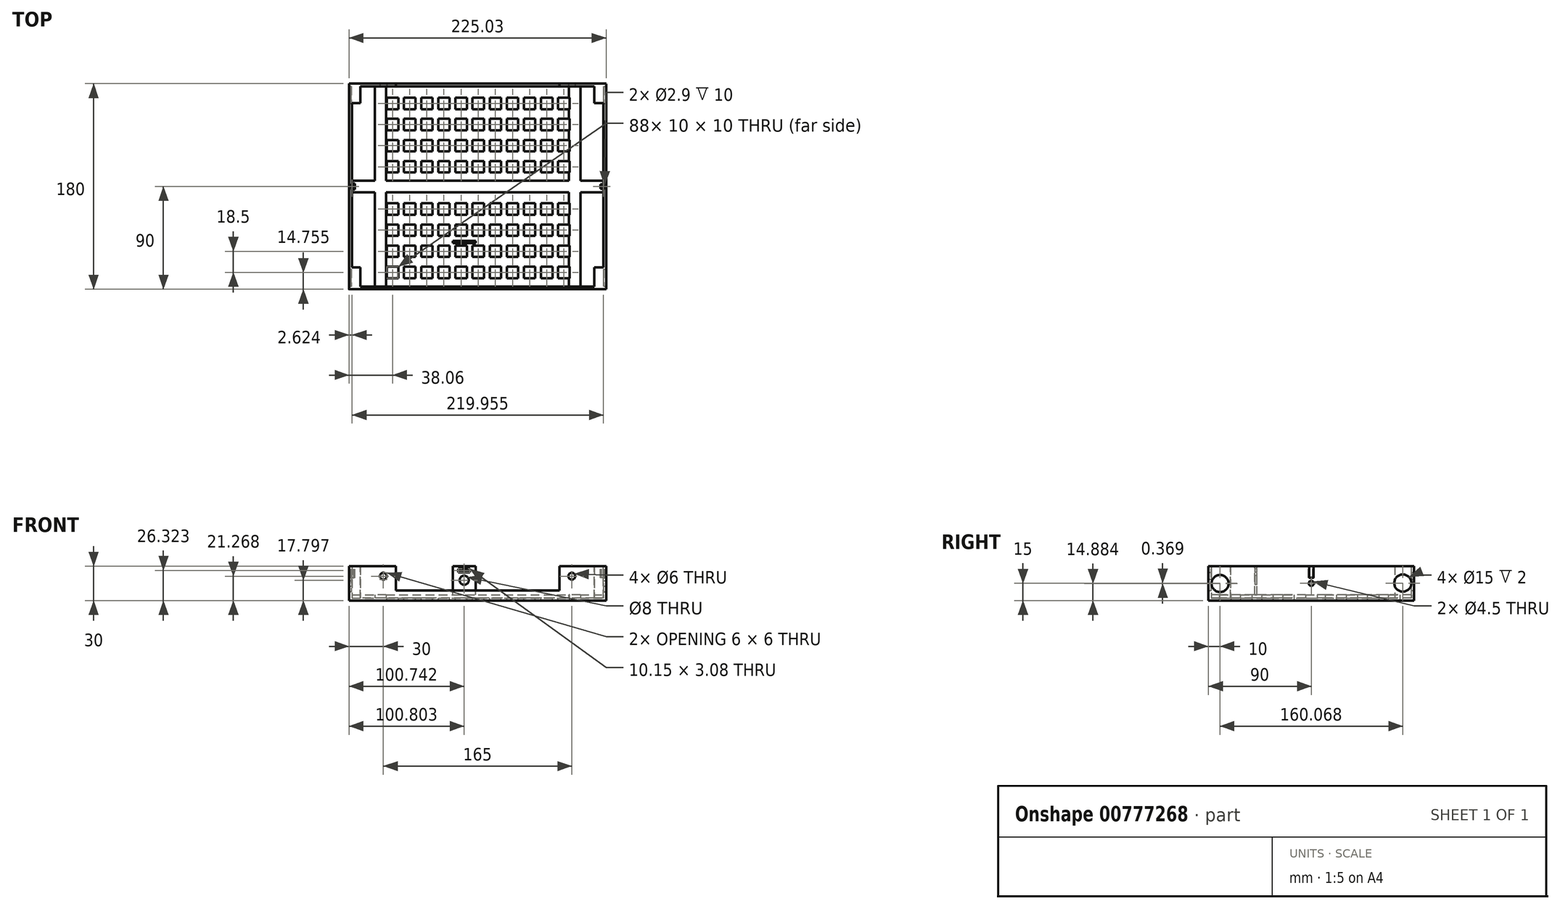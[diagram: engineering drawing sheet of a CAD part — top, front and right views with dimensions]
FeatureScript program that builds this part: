
annotation { "Feature Type Name" : "Feature", "Feature Type Description" : "" }
export const myFeature = defineFeature(function(context is Context, id is Id, definition is map)
    precondition{}
    {
        {
            var Q0;
            Q0=qCreatedBy(makeId("Top.planeOp"),FACE);
            var sketch = newSketch(context, id + "F0", { "sketchPlane" : qUnion([Q0])});
            skLineSegment(sketch, "E0.bottom", {"start": v(112.5, -90) * mm, "end": v(-112.5, -90) * mm});
            skLineSegment(sketch, "E0.top", {"start": v(112.5, 90) * mm, "end": v(-112.5, 90) * mm});
            skLineSegment(sketch, "E0.left", {"start": v(112.5, -90) * mm, "end": v(112.5, 90) * mm});
            skLineSegment(sketch, "E0.right", {"start": v(-112.5, -90) * mm, "end": v(-112.5, 90) * mm});
            skPoint(sketch, "E0.middle", {"position": v(0, 0) * mm});
            skSolve(sketch);
        }
        {
            var Q0;
            Q0=makeQuery(id+"F0.imprint","IMPRINT",FACE,{"disambiguationData":[TD([[makeQuery(id+"F0.imprint","IMPRINT",EDGE,{"derivedFrom":sQuery(id+"F0.wireOp",EDGE,"E0.bottom")}),-1.0]])]});
            extrude(context, id + "F1", {"entities" : qUnion([Q0]), "depth" : 30 * mm, "offsetDistance" : 25 * mm});
        }
        {
            var Q0;
            Q0=makeQuery(id+"F1.opExtrude","CAP_FACE",FACE,{"disambiguationData":[OSD([sQuery(id+"F0.wireOp",EDGE,"E0.bottom"),sQuery(id+"F0.wireOp",EDGE,"E0.top"),sQuery(id+"F0.wireOp",EDGE,"E0.left"),sQuery(id+"F0.wireOp",EDGE,"E0.right")])],"isStart":false});
            var sketch = newSketch(context, id + "F2", { "sketchPlane" : qUnion([Q0])});
            skLineSegment(sketch, "E1.bottom", {"start": v(110, -87.5) * mm, "end": v(-110, -87.5) * mm});
            skLineSegment(sketch, "E1.top", {"start": v(110, 87.5) * mm, "end": v(-110, 87.5) * mm});
            skLineSegment(sketch, "E1.left", {"start": v(110, -87.5) * mm, "end": v(110, 87.5) * mm});
            skLineSegment(sketch, "E1.right", {"start": v(-110, -87.5) * mm, "end": v(-110, 87.5) * mm});
            skPoint(sketch, "E1.middle", {"position": v(0, 0) * mm});
            skSolve(sketch);
        }
        {
            var Q0;
            Q0=makeQuery(id+"F2.imprint","IMPRINT",FACE,{"disambiguationData":[TD([[makeQuery(id+"F2.imprint","IMPRINT",EDGE,{"derivedFrom":sQuery(id+"F2.wireOp",EDGE,"E1.bottom")}),-1.0]])]});
            extrude(context, id + "F3", {"entities" : qUnion([Q0]), "operationType" : NewBodyOperationType.REMOVE, "oppositeDirection" : true, "depth" : 28 * mm, "offsetDistance" : 25 * mm});
        }
        {
            var Q0;
            Q0=makeQuery(id+"F1.opExtrude","SWEPT_FACE",FACE,{"disambiguationData":[OSD([sQuery(id+"F0.wireOp",EDGE,"E0.bottom")])]});
            var sketch = newSketch(context, id + "F4", { "sketchPlane" : qUnion([Q0])});
            skLineSegment(sketch, "E2", {"start": v(0, 15) * mm, "end": v(0, 30) * mm, "construction": true});
            skPoint(sketch, "E2.startSnap0", {"position": v(-112.5, 15) * mm});
            skPoint(sketch, "E2.startSnap1", {"position": v(0, 30) * mm});
            skLineSegment(sketch, "E3", {"start": v(0, 15) * mm, "end": v(-112.5, 15) * mm, "construction": true});
            skLineSegment(sketch, "E4", {"start": v(0, 15) * mm, "end": v(112.5, 15) * mm, "construction": true});
            skLineSegment(sketch, "E5", {"start": v(-112.5, 0) * mm, "end": v(-82.5, 0) * mm, "construction": true});
            skLineSegment(sketch, "E6", {"start": v(112.5, 0) * mm, "end": v(82.5, 0) * mm, "construction": true});
            skLineSegment(sketch, "E7", {"start": v(-82.5, 0) * mm, "end": v(-82.5, 30) * mm, "construction": true});
            skLineSegment(sketch, "E8", {"start": v(82.5, 0) * mm, "end": v(82.5, 30) * mm, "construction": true});
            skLineSegment(sketch, "E9", {"start": v(-112.5, 30) * mm, "end": v(-72.5, 30) * mm, "construction": true});
            skLineSegment(sketch, "E10", {"start": v(112.5, 30) * mm, "end": v(72.5, 30) * mm, "construction": true});
            skLineSegment(sketch, "E11", {"start": v(-112.5, 0) * mm, "end": v(-112.5, 10) * mm, "construction": true});
            skLineSegment(sketch, "E12", {"start": v(-112.5, 10) * mm, "end": v(112.5, 10) * mm, "construction": true});
            skLineSegment(sketch, "E13", {"start": v(-22.5, 30) * mm, "end": v(-22.5, 0) * mm, "construction": true});
            skLineSegment(sketch, "E14", {"start": v(22.5, 30) * mm, "end": v(22.5, 0) * mm, "construction": true});
            skFitSpline(sketch, "E15", {"points": [v(-72.5, 30) * mm, v(-71.2, 15) * mm, v(-22.5, 10) * mm], "startDerivative": vector(-3.64, -53.35) * mm, "endDerivative": vector(76.18, -37.14) * mm});
            skFitSpline(sketch, "E16", {"points": [v(72.5, 30) * mm, v(72.49, 15) * mm, v(22.5, 10) * mm], "startDerivative": vector(-2.42, -56.98) * mm, "endDerivative": vector(-66.73, -35.72) * mm});
            skLineSegment(sketch, "E17", {"start": v(-22.5, 10) * mm, "end": v(-22.5, 0) * mm});
            skLineSegment(sketch, "E18", {"start": v(22.5, 10) * mm, "end": v(22.5, 0) * mm});
            skLineSegment(sketch, "E19", {"start": v(-22.5, 10) * mm, "end": v(22.5, 10) * mm});
            skLineSegment(sketch, "E20", {"start": v(112.5, 21.27) * mm, "end": v(-112.5, 21.27) * mm, "construction": true});
            skCircle(sketch, "E21", {"center": v(82.5, 21.27) * mm, "radius": 3 * mm});
            skCircle(sketch, "E22", {"center": v(-82.5, 21.27) * mm, "radius": 3 * mm});
            skSolve(sketch);
        }
        {
            var Q0;
            Q0=qSketchRegion(id+"F4",true);
            extrude(context, id + "F5", {"entities" : qUnion([Q0]), "operationType" : NewBodyOperationType.REMOVE, "oppositeDirection" : true, "depth" : 2500 * mm, "offsetDistance" : 25 * mm});
        }
        {
            var Q0;
            Q0=makeQuery(id+"F3.boolean.opBoolean","COPY",FACE,{"derivedFrom":makeQuery(id+"F3.opExtrude","CAP_FACE",FACE,{"disambiguationData":[OSD([sQuery(id+"F2.wireOp",EDGE,"E1.bottom"),sQuery(id+"F2.wireOp",EDGE,"E1.top"),sQuery(id+"F2.wireOp",EDGE,"E1.left"),sQuery(id+"F2.wireOp",EDGE,"E1.right")])],"isStart":false})});
            var sketch = newSketch(context, id + "F6", { "sketchPlane" : qUnion([Q0])});
            skLineSegment(sketch, "E23", {"start": v(-110, 87.5) * mm, "end": v(-90, 87.5) * mm, "construction": true});
            skLineSegment(sketch, "E24.bottom", {"start": v(-90, 87.5) * mm, "end": v(-80, 87.5) * mm});
            skLineSegment(sketch, "E24.top", {"start": v(-90, -87.5) * mm, "end": v(-80, -87.5) * mm});
            skLineSegment(sketch, "E24.left", {"start": v(-90, 87.5) * mm, "end": v(-90, -87.5) * mm});
            skLineSegment(sketch, "E24.right", {"start": v(-80, 87.5) * mm, "end": v(-80, -87.5) * mm});
            skLineSegment(sketch, "E25", {"start": v(110, 87.5) * mm, "end": v(90, 87.5) * mm, "construction": true});
            skLineSegment(sketch, "E26.bottom", {"start": v(90, 87.5) * mm, "end": v(80, 87.5) * mm});
            skLineSegment(sketch, "E26.top", {"start": v(90, -87.5) * mm, "end": v(80, -87.5) * mm});
            skLineSegment(sketch, "E26.left", {"start": v(90, 87.5) * mm, "end": v(90, -87.5) * mm});
            skLineSegment(sketch, "E26.right", {"start": v(80, 87.5) * mm, "end": v(80, -87.5) * mm});
            skLineSegment(sketch, "E27.bottom", {"start": v(-110, 5) * mm, "end": v(110, 5) * mm});
            skLineSegment(sketch, "E27.top", {"start": v(-110, -5) * mm, "end": v(110, -5) * mm});
            skLineSegment(sketch, "E27.left", {"start": v(-110, 5) * mm, "end": v(-110, -5) * mm});
            skLineSegment(sketch, "E27.right", {"start": v(110, 5) * mm, "end": v(110, -5) * mm});
            skPoint(sketch, "E27.middle", {"position": v(0, 0) * mm});
            skSolve(sketch);
        }
        {
            var Q0;
            Q0=makeQuery(id+"F6.imprint","IMPRINT",FACE,{"disambiguationData":[TD([[makeQuery(id+"F6.imprint","IMPRINT",EDGE,{"derivedFrom":sQuery(id+"F6.wireOp",EDGE,"E24.bottom")}),1.0]])]});
            var Q1;
            Q1=makeQuery(id+"F6.imprint","IMPRINT",FACE,{"disambiguationData":[TD([[makeQuery(id+"F6.imprint","IMPRINT",EDGE,{"derivedFrom":sQuery(id+"F6.wireOp",EDGE,"E26.bottom")}),1.0]])]});
            var Q2;
            {var subQ5=sQuery(id+"F6.wireOp",EDGE,"E27.left");Q2=makeQuery(id+"F6.imprint","IMPRINT",FACE,{"disambiguationData":[TD([[makeQuery(id+"F6.imprint","IMPRINT",EDGE,{"derivedFrom":subQ5}),-1.0]])]});}
            var Q3;
            {var subQ0=sQuery(id+"F6.wireOp",EDGE,"E27.bottom");var subQ1=sQuery(id+"F6.wireOp",EDGE,"E24.left");var subQ2=makeQuery(id+"F6.imprint","INTERSECT",VERTEX,{"derivedFrom":[subQ1,subQ0]});Q3=makeQuery(id+"F6.imprint","IMPRINT",FACE,{"disambiguationData":[TD([[makeQuery(id+"F6.imprint","IMPRINT",EDGE,{"disambiguationData":[TD([[subQ2,-1.0]])],"derivedFrom":subQ1}),1.0]])]});}
            var Q4;
            {var subQ0=sQuery(id+"F6.wireOp",EDGE,"E24.top");Q4=makeQuery(id+"F6.imprint","IMPRINT",FACE,{"disambiguationData":[TD([[makeQuery(id+"F6.imprint","IMPRINT",EDGE,{"derivedFrom":subQ0}),-1.0]])]});}
            var Q5;
            {var subQ0=sQuery(id+"F6.wireOp",EDGE,"E27.bottom");var subQ1=sQuery(id+"F6.wireOp",EDGE,"E24.right");var subQ2=makeQuery(id+"F6.imprint","INTERSECT",VERTEX,{"derivedFrom":[subQ1,subQ0]});Q5=makeQuery(id+"F6.imprint","IMPRINT",FACE,{"disambiguationData":[TD([[makeQuery(id+"F6.imprint","IMPRINT",EDGE,{"disambiguationData":[TD([[subQ2,-1.0]])],"derivedFrom":subQ1}),1.0]])]});}
            var Q6;
            {var subQ0=sQuery(id+"F6.wireOp",EDGE,"E27.bottom");var subQ1=sQuery(id+"F6.wireOp",EDGE,"E26.left");var subQ2=makeQuery(id+"F6.imprint","INTERSECT",VERTEX,{"derivedFrom":[subQ1,subQ0]});Q6=makeQuery(id+"F6.imprint","IMPRINT",FACE,{"disambiguationData":[TD([[makeQuery(id+"F6.imprint","IMPRINT",EDGE,{"disambiguationData":[TD([[subQ2,-1.0]])],"derivedFrom":subQ1}),-1.0]])]});}
            var Q7;
            {var subQ0=sQuery(id+"F6.wireOp",EDGE,"E26.top");Q7=makeQuery(id+"F6.imprint","IMPRINT",FACE,{"disambiguationData":[TD([[makeQuery(id+"F6.imprint","IMPRINT",EDGE,{"derivedFrom":subQ0}),-1.0]])]});}
            var Q8;
            {var subQ5=sQuery(id+"F6.wireOp",EDGE,"E27.right");Q8=makeQuery(id+"F6.imprint","IMPRINT",FACE,{"disambiguationData":[TD([[makeQuery(id+"F6.imprint","IMPRINT",EDGE,{"derivedFrom":subQ5}),1.0]])]});}
            extrude(context, id + "F7", {"entities" : qUnion([Q0, Q1, Q2, Q3, Q4, Q5, Q6, Q7, Q8]), "depth" : 3 * mm, "offsetDistance" : 25 * mm});
        }
        {
            var Q0;
            Q0=makeQuery(id+"F1.opExtrude","SWEPT_FACE",FACE,{"disambiguationData":[OSD([sQuery(id+"F0.wireOp",EDGE,"E0.left")])]});
            var sketch = newSketch(context, id + "F8", { "sketchPlane" : qUnion([Q0])});
            skLineSegment(sketch, "E28", {"start": v(0, 30) * mm, "end": v(0, 0) * mm, "construction": true});
            skLineSegment(sketch, "E29", {"start": v(-90, 15) * mm, "end": v(90, 15) * mm, "construction": true});
            skCircle(sketch, "E30", {"center": v(0, 15) * mm, "radius": 2.25 * mm});
            skSolve(sketch);
        }
        {
            var Q0;
            Q0=makeQuery(id+"F8.imprint","IMPRINT",FACE,{"disambiguationData":[TD([[makeQuery(id+"F8.imprint","IMPRINT",EDGE,{"derivedFrom":sQuery(id+"F8.wireOp",EDGE,"E30")}),1.0]])]});
            extrude(context, id + "F9", {"entities" : qUnion([Q0]), "operationType" : NewBodyOperationType.REMOVE, "endBound" : BoundingType.THROUGH_ALL, "oppositeDirection" : true, "depth" : 25 * mm, "offsetDistance" : 25 * mm});
        }
        {
            var Q0;
            Q0=makeQuery(id+"F1.opExtrude","SWEPT_FACE",FACE,{"disambiguationData":[OSD([sQuery(id+"F0.wireOp",EDGE,"E0.top")])]});
            var sketch = newSketch(context, id + "F10", { "sketchPlane" : qUnion([Q0])});
            skLineSegment(sketch, "E31.bottom", {"start": v(71.59, 8.69) * mm, "end": v(-71.59, 8.69) * mm});
            skLineSegment(sketch, "E31.top", {"start": v(71.59, 51.31) * mm, "end": v(-71.59, 51.31) * mm});
            skLineSegment(sketch, "E31.left", {"start": v(71.59, 8.69) * mm, "end": v(71.59, 51.31) * mm});
            skLineSegment(sketch, "E31.right", {"start": v(-71.59, 8.69) * mm, "end": v(-71.59, 51.31) * mm});
            skPoint(sketch, "E31.middle", {"position": v(0, 30) * mm});
            skSolve(sketch);
        }
        {
            var Q0;
            {var subQ0=sQuery(id+"F10.wireOp",EDGE,"E31.bottom");Q0=makeQuery(id+"F10.imprint","IMPRINT",FACE,{"disambiguationData":[TD([[makeQuery(id+"F10.imprint","IMPRINT",EDGE,{"derivedFrom":subQ0}),-1.0]])]});}
            extrude(context, id + "F11", {"entities" : qUnion([Q0]), "operationType" : NewBodyOperationType.REMOVE, "oppositeDirection" : true, "depth" : 3000 * mm, "offsetDistance" : 25 * mm});
        }
        {
            var Q0;
            Q0=makeQuery(id+"F2.imprint","IMPRINT",FACE,{"disambiguationData":[TD([[makeQuery(id+"F2.imprint","IMPRINT",EDGE,{"derivedFrom":sQuery(id+"F2.wireOp",EDGE,"E1.bottom")}),-1.0]])]});
            var sketch = newSketch(context, id + "F12", { "sketchPlane" : qUnion([Q0])});
            skLineSegment(sketch, "E32.bottom", {"start": v(-112.4, 89.96) * mm, "end": v(-102.7, 89.96) * mm});
            skLineSegment(sketch, "E32.top", {"start": v(-112.4, 72.97) * mm, "end": v(-102.7, 72.97) * mm});
            skLineSegment(sketch, "E32.left", {"start": v(-112.4, 89.96) * mm, "end": v(-112.4, 72.97) * mm});
            skLineSegment(sketch, "E32.right", {"start": v(-102.7, 89.96) * mm, "end": v(-102.7, 72.97) * mm});
            skLineSegment(sketch, "E33.bottom", {"start": v(-112.5, -89.96) * mm, "end": v(-102.68, -89.96) * mm});
            skLineSegment(sketch, "E33.top", {"start": v(-112.5, -70.82) * mm, "end": v(-102.68, -70.82) * mm});
            skLineSegment(sketch, "E33.left", {"start": v(-112.5, -89.96) * mm, "end": v(-112.5, -70.82) * mm});
            skLineSegment(sketch, "E33.right", {"start": v(-102.68, -89.96) * mm, "end": v(-102.68, -70.82) * mm});
            skLineSegment(sketch, "E34.bottom", {"start": v(112.5, 89.98) * mm, "end": v(102.19, 89.98) * mm});
            skLineSegment(sketch, "E34.top", {"start": v(112.5, 72.97) * mm, "end": v(102.19, 72.97) * mm});
            skLineSegment(sketch, "E34.left", {"start": v(112.5, 89.98) * mm, "end": v(112.5, 72.97) * mm});
            skLineSegment(sketch, "E34.right", {"start": v(102.19, 89.98) * mm, "end": v(102.19, 72.97) * mm});
            skLineSegment(sketch, "E35.bottom", {"start": v(112.45, -89.96) * mm, "end": v(102.2, -89.96) * mm});
            skLineSegment(sketch, "E35.top", {"start": v(112.45, -70.67) * mm, "end": v(102.2, -70.67) * mm});
            skLineSegment(sketch, "E35.left", {"start": v(112.45, -89.96) * mm, "end": v(112.45, -70.67) * mm});
            skLineSegment(sketch, "E35.right", {"start": v(102.2, -89.96) * mm, "end": v(102.2, -70.67) * mm});
            skLineSegment(sketch, "E36", {"start": v(-102.7, -93.75) * mm, "end": v(-102.7, 94.08) * mm, "construction": true});
            skLineSegment(sketch, "E37", {"start": v(-116.28, -70.82) * mm, "end": v(124.38, -70.82) * mm, "construction": true});
            skLineSegment(sketch, "E38", {"start": v(-119.93, 72.97) * mm, "end": v(152.22, 72.97) * mm, "construction": true});
            skLineSegment(sketch, "E39", {"start": v(102.19, 97.41) * mm, "end": v(102.19, -106.67) * mm, "construction": true});
            skSolve(sketch);
        }
        {
            var Q0;
            Q0=qSketchRegion(id+"F12",true);
            extrude(context, id + "F13", {"entities" : qUnion([Q0]), "operationType" : NewBodyOperationType.ADD, "oppositeDirection" : true, "depth" : 30 * mm, "offsetDistance" : 25 * mm});
        }
        {
            var Q0;
            Q0=makeQuery(id+"F1.opExtrude","SWEPT_FACE",FACE,{"disambiguationData":[OSD([sQuery(id+"F0.wireOp",EDGE,"E0.right")])]});
            var sketch = newSketch(context, id + "F14", { "sketchPlane" : qUnion([Q0])});
            skLineSegment(sketch, "E40", {"start": v(-80, 30) * mm, "end": v(-80, 0) * mm, "construction": true});
            skLineSegment(sketch, "E41", {"start": v(80, 30) * mm, "end": v(80, 0) * mm, "construction": true});
            skCircle(sketch, "E42", {"center": v(-80, 15) * mm, "radius": 7.5 * mm});
            skCircle(sketch, "E43", {"center": v(80, 15) * mm, "radius": 7.5 * mm});
            skSolve(sketch);
        }
        {
            var Q0;
            Q0=qSketchRegion(id+"F14",true);
            extrude(context, id + "F15", {"entities" : qUnion([Q0]), "operationType" : NewBodyOperationType.REMOVE, "oppositeDirection" : true, "depth" : 2 * mm, "offsetDistance" : 25 * mm});
        }
        {
            var Q0;
            Q0=makeQuery(id+"F8.imprint","IMPRINT",FACE,{"disambiguationData":[TD([[makeQuery(id+"F8.imprint","IMPRINT",EDGE,{"derivedFrom":sQuery(id+"F8.wireOp",EDGE,"E30")}),-1.0]])]});
            var sketch = newSketch(context, id + "F16", { "sketchPlane" : qUnion([Q0])});
            skCircle(sketch, "E44", {"center": v(-79.9, 14.88) * mm, "radius": 7.5 * mm});
            skCircle(sketch, "E45", {"center": v(80.07, 15.25) * mm, "radius": 7.5 * mm});
            skSolve(sketch);
        }
        {
            var Q0;
            Q0=qSketchRegion(id+"F16",true);
            extrude(context, id + "F17", {"entities" : qUnion([Q0]), "operationType" : NewBodyOperationType.REMOVE, "oppositeDirection" : true, "depth" : 2 * mm, "offsetDistance" : 25 * mm});
        }
        {
            var Q0;
            {var subQ0=sQuery(id+"F12.wireOp",EDGE,"E32.right");var subQ17=sQuery(id+"F12.wireOp",EDGE,"E32.top");var subQ18=makeQuery(id+"F12.imprint","INTERSECT",VERTEX,{"derivedFrom":[subQ17,subQ0]});Q0=makeQuery(id+"F12.imprint","IMPRINT",FACE,{"disambiguationData":[TD([[makeQuery(id+"F12.imprint","IMPRINT",EDGE,{"disambiguationData":[TD([[subQ18,1.0]])],"derivedFrom":subQ17}),-1.0]])]});}
            var sketch = newSketch(context, id + "F18", { "sketchPlane" : qUnion([Q0])});
            skLineSegment(sketch, "E46", {"start": v(-21.73, -47.51) * mm, "end": v(-1.73, -47.51) * mm});
            skLineSegment(sketch, "E47", {"start": v(-1.73, -47.51) * mm, "end": v(-1.73, -49.51) * mm});
            skLineSegment(sketch, "E48", {"start": v(-1.73, -49.51) * mm, "end": v(-21.73, -49.51) * mm});
            skLineSegment(sketch, "E49", {"start": v(-21.73, -49.51) * mm, "end": v(-21.73, -47.51) * mm});
            skSolve(sketch);
        }
        {
            var Q0;
            Q0=makeQuery(id+"F18.imprint","IMPRINT",FACE,{"disambiguationData":[TD([[makeQuery(id+"F18.imprint","IMPRINT",EDGE,{"derivedFrom":sQuery(id+"F18.wireOp",EDGE,"E46")}),-1.0]])]});
            extrude(context, id + "F19", {"entities" : qUnion([Q0]), "operationType" : NewBodyOperationType.ADD, "oppositeDirection" : true, "depth" : 25 * mm, "offsetDistance" : 25 * mm});
        }
        {
            var Q0;
            {var subQ0=sQuery(id+"F4.wireOp",EDGE,"E15");Q0=makeQuery(id+"F4.imprint","IMPRINT",FACE,{"disambiguationData":[TD([[makeQuery(id+"F4.imprint","IMPRINT",EDGE,{"derivedFrom":subQ0}),1.0]])]});}
            var sketch = newSketch(context, id + "F20", { "sketchPlane" : qUnion([Q0])});
            skCircle(sketch, "E50", {"center": v(-11.7, 17.8) * mm, "radius": 4 * mm});
            skSolve(sketch);
        }
        {
            var Q0;
            Q0=qSketchRegion(id+"F20",true);
            extrude(context, id + "F21", {"entities" : qUnion([Q0]), "operationType" : NewBodyOperationType.REMOVE, "oppositeDirection" : true, "depth" : 3000 * mm, "offsetDistance" : 25 * mm});
        }
        {
            var Q0;
            {var subQ4=sQuery(id+"F4.wireOp",EDGE,"E15");Q0=makeQuery(id+"F4.imprint","IMPRINT",FACE,{"disambiguationData":[TD([[makeQuery(id+"F4.imprint","IMPRINT",EDGE,{"derivedFrom":subQ4}),-1.0]])]});}
            var sketch = newSketch(context, id + "F22", { "sketchPlane" : qUnion([Q0])});
            skLineSegment(sketch, "E51.bottom", {"start": v(-6.68, 24.78) * mm, "end": v(-16.83, 24.78) * mm});
            skLineSegment(sketch, "E51.top", {"start": v(-6.68, 27.86) * mm, "end": v(-16.83, 27.86) * mm});
            skLineSegment(sketch, "E51.left", {"start": v(-6.68, 24.78) * mm, "end": v(-6.68, 27.86) * mm});
            skLineSegment(sketch, "E51.right", {"start": v(-16.83, 24.78) * mm, "end": v(-16.83, 27.86) * mm});
            skPoint(sketch, "E51.middle", {"position": v(-11.76, 26.32) * mm});
            skSolve(sketch);
        }
        {
            var Q0;
            Q0=qSketchRegion(id+"F22",true);
            extrude(context, id + "F23", {"entities" : qUnion([Q0]), "operationType" : NewBodyOperationType.REMOVE, "oppositeDirection" : true, "depth" : 3000 * mm, "offsetDistance" : 25 * mm});
        }
        {
            var Q0;
            Q0=makeQuery(id+"F0.imprint","IMPRINT",FACE,{"disambiguationData":[TD([[makeQuery(id+"F0.imprint","IMPRINT",EDGE,{"derivedFrom":sQuery(id+"F0.wireOp",EDGE,"E0.bottom")}),-1.0]])]});
            var sketch = newSketch(context, id + "F24", { "sketchPlane" : qUnion([Q0])});
            skLineSegment(sketch, "E52.bottom", {"start": v(-69.44, -80.25) * mm, "end": v(-79.44, -80.25) * mm});
            skLineSegment(sketch, "E52.top", {"start": v(-69.44, -70.25) * mm, "end": v(-79.44, -70.25) * mm});
            skLineSegment(sketch, "E52.left", {"start": v(-69.44, -80.25) * mm, "end": v(-69.44, -70.25) * mm});
            skLineSegment(sketch, "E52.right", {"start": v(-79.44, -80.25) * mm, "end": v(-79.44, -70.25) * mm});
            skPoint(sketch, "E52.middle", {"position": v(-74.44, -75.25) * mm});
            skPoint(sketch, "E53.0.1.0", {"position": v(-74.44, -56.75) * mm});
            skLineSegment(sketch, "E53.0.1.1", {"start": v(-69.44, -61.75) * mm, "end": v(-69.44, -51.75) * mm});
            skLineSegment(sketch, "E53.0.1.2", {"start": v(-69.44, -51.75) * mm, "end": v(-79.44, -51.75) * mm});
            skLineSegment(sketch, "E53.0.1.3", {"start": v(-69.44, -61.75) * mm, "end": v(-79.44, -61.75) * mm});
            skLineSegment(sketch, "E53.0.1.4", {"start": v(-79.44, -61.75) * mm, "end": v(-79.44, -51.75) * mm});
            skPoint(sketch, "E53.0.2.0", {"position": v(-74.44, -38.25) * mm});
            skLineSegment(sketch, "E53.0.2.1", {"start": v(-69.44, -43.25) * mm, "end": v(-69.44, -33.25) * mm});
            skLineSegment(sketch, "E53.0.2.2", {"start": v(-69.44, -33.25) * mm, "end": v(-79.44, -33.25) * mm});
            skLineSegment(sketch, "E53.0.2.3", {"start": v(-69.44, -43.25) * mm, "end": v(-79.44, -43.25) * mm});
            skLineSegment(sketch, "E53.0.2.4", {"start": v(-79.44, -43.25) * mm, "end": v(-79.44, -33.25) * mm});
            skPoint(sketch, "E53.0.3.0", {"position": v(-74.44, -19.75) * mm});
            skLineSegment(sketch, "E53.0.3.1", {"start": v(-69.44, -24.75) * mm, "end": v(-69.44, -14.75) * mm});
            skLineSegment(sketch, "E53.0.3.2", {"start": v(-69.44, -14.75) * mm, "end": v(-79.44, -14.75) * mm});
            skLineSegment(sketch, "E53.0.3.3", {"start": v(-69.44, -24.75) * mm, "end": v(-79.44, -24.75) * mm});
            skLineSegment(sketch, "E53.0.3.4", {"start": v(-79.44, -24.75) * mm, "end": v(-79.44, -14.75) * mm});
            skPoint(sketch, "E53.0.5.0", {"position": v(-74.44, 17.25) * mm});
            skLineSegment(sketch, "E53.0.5.1", {"start": v(-69.44, 12.25) * mm, "end": v(-69.44, 22.25) * mm});
            skLineSegment(sketch, "E53.0.5.2", {"start": v(-69.44, 22.25) * mm, "end": v(-79.44, 22.25) * mm});
            skLineSegment(sketch, "E53.0.5.3", {"start": v(-69.44, 12.25) * mm, "end": v(-79.44, 12.25) * mm});
            skLineSegment(sketch, "E53.0.5.4", {"start": v(-79.44, 12.25) * mm, "end": v(-79.44, 22.25) * mm});
            skPoint(sketch, "E53.0.6.0", {"position": v(-74.44, 35.75) * mm});
            skLineSegment(sketch, "E53.0.6.1", {"start": v(-69.44, 30.75) * mm, "end": v(-69.44, 40.75) * mm});
            skLineSegment(sketch, "E53.0.6.2", {"start": v(-69.44, 40.75) * mm, "end": v(-79.44, 40.75) * mm});
            skLineSegment(sketch, "E53.0.6.3", {"start": v(-69.44, 30.75) * mm, "end": v(-79.44, 30.75) * mm});
            skLineSegment(sketch, "E53.0.6.4", {"start": v(-79.44, 30.75) * mm, "end": v(-79.44, 40.75) * mm});
            skPoint(sketch, "E53.0.7.0", {"position": v(-74.44, 54.25) * mm});
            skLineSegment(sketch, "E53.0.7.1", {"start": v(-69.44, 49.25) * mm, "end": v(-69.44, 59.25) * mm});
            skLineSegment(sketch, "E53.0.7.2", {"start": v(-69.44, 59.25) * mm, "end": v(-79.44, 59.25) * mm});
            skLineSegment(sketch, "E53.0.7.3", {"start": v(-69.44, 49.25) * mm, "end": v(-79.44, 49.25) * mm});
            skLineSegment(sketch, "E53.0.7.4", {"start": v(-79.44, 49.25) * mm, "end": v(-79.44, 59.25) * mm});
            skPoint(sketch, "E53.0.8.0", {"position": v(-74.44, 72.75) * mm});
            skLineSegment(sketch, "E53.0.8.1", {"start": v(-69.44, 67.75) * mm, "end": v(-69.44, 77.75) * mm});
            skLineSegment(sketch, "E53.0.8.2", {"start": v(-69.44, 77.75) * mm, "end": v(-79.44, 77.75) * mm});
            skLineSegment(sketch, "E53.0.8.3", {"start": v(-69.44, 67.75) * mm, "end": v(-79.44, 67.75) * mm});
            skLineSegment(sketch, "E53.0.8.4", {"start": v(-79.44, 67.75) * mm, "end": v(-79.44, 77.75) * mm});
            skPoint(sketch, "E53.1.0.0", {"position": v(-59.44, -75.25) * mm});
            skLineSegment(sketch, "E53.1.0.1", {"start": v(-54.44, -80.25) * mm, "end": v(-54.44, -70.25) * mm});
            skLineSegment(sketch, "E53.1.0.2", {"start": v(-54.44, -70.25) * mm, "end": v(-64.44, -70.25) * mm});
            skLineSegment(sketch, "E53.1.0.3", {"start": v(-54.44, -80.25) * mm, "end": v(-64.44, -80.25) * mm});
            skLineSegment(sketch, "E53.1.0.4", {"start": v(-64.44, -80.25) * mm, "end": v(-64.44, -70.25) * mm});
            skPoint(sketch, "E53.1.1.0", {"position": v(-59.44, -56.75) * mm});
            skLineSegment(sketch, "E53.1.1.1", {"start": v(-54.44, -61.75) * mm, "end": v(-54.44, -51.75) * mm});
            skLineSegment(sketch, "E53.1.1.2", {"start": v(-54.44, -51.75) * mm, "end": v(-64.44, -51.75) * mm});
            skLineSegment(sketch, "E53.1.1.3", {"start": v(-54.44, -61.75) * mm, "end": v(-64.44, -61.75) * mm});
            skLineSegment(sketch, "E53.1.1.4", {"start": v(-64.44, -61.75) * mm, "end": v(-64.44, -51.75) * mm});
            skPoint(sketch, "E53.1.2.0", {"position": v(-59.44, -38.25) * mm});
            skLineSegment(sketch, "E53.1.2.1", {"start": v(-54.44, -43.25) * mm, "end": v(-54.44, -33.25) * mm});
            skLineSegment(sketch, "E53.1.2.2", {"start": v(-54.44, -33.25) * mm, "end": v(-64.44, -33.25) * mm});
            skLineSegment(sketch, "E53.1.2.3", {"start": v(-54.44, -43.25) * mm, "end": v(-64.44, -43.25) * mm});
            skLineSegment(sketch, "E53.1.2.4", {"start": v(-64.44, -43.25) * mm, "end": v(-64.44, -33.25) * mm});
            skPoint(sketch, "E53.1.3.0", {"position": v(-59.44, -19.75) * mm});
            skLineSegment(sketch, "E53.1.3.1", {"start": v(-54.44, -24.75) * mm, "end": v(-54.44, -14.75) * mm});
            skLineSegment(sketch, "E53.1.3.2", {"start": v(-54.44, -14.75) * mm, "end": v(-64.44, -14.75) * mm});
            skLineSegment(sketch, "E53.1.3.3", {"start": v(-54.44, -24.75) * mm, "end": v(-64.44, -24.75) * mm});
            skLineSegment(sketch, "E53.1.3.4", {"start": v(-64.44, -24.75) * mm, "end": v(-64.44, -14.75) * mm});
            skPoint(sketch, "E53.1.5.0", {"position": v(-59.44, 17.25) * mm});
            skLineSegment(sketch, "E53.1.5.1", {"start": v(-54.44, 12.25) * mm, "end": v(-54.44, 22.25) * mm});
            skLineSegment(sketch, "E53.1.5.2", {"start": v(-54.44, 22.25) * mm, "end": v(-64.44, 22.25) * mm});
            skLineSegment(sketch, "E53.1.5.3", {"start": v(-54.44, 12.25) * mm, "end": v(-64.44, 12.25) * mm});
            skLineSegment(sketch, "E53.1.5.4", {"start": v(-64.44, 12.25) * mm, "end": v(-64.44, 22.25) * mm});
            skPoint(sketch, "E53.1.6.0", {"position": v(-59.44, 35.75) * mm});
            skLineSegment(sketch, "E53.1.6.1", {"start": v(-54.44, 30.75) * mm, "end": v(-54.44, 40.75) * mm});
            skLineSegment(sketch, "E53.1.6.2", {"start": v(-54.44, 40.75) * mm, "end": v(-64.44, 40.75) * mm});
            skLineSegment(sketch, "E53.1.6.3", {"start": v(-54.44, 30.75) * mm, "end": v(-64.44, 30.75) * mm});
            skLineSegment(sketch, "E53.1.6.4", {"start": v(-64.44, 30.75) * mm, "end": v(-64.44, 40.75) * mm});
            skPoint(sketch, "E53.1.7.0", {"position": v(-59.44, 54.25) * mm});
            skLineSegment(sketch, "E53.1.7.1", {"start": v(-54.44, 49.25) * mm, "end": v(-54.44, 59.25) * mm});
            skLineSegment(sketch, "E53.1.7.2", {"start": v(-54.44, 59.25) * mm, "end": v(-64.44, 59.25) * mm});
            skLineSegment(sketch, "E53.1.7.3", {"start": v(-54.44, 49.25) * mm, "end": v(-64.44, 49.25) * mm});
            skLineSegment(sketch, "E53.1.7.4", {"start": v(-64.44, 49.25) * mm, "end": v(-64.44, 59.25) * mm});
            skPoint(sketch, "E53.1.8.0", {"position": v(-59.44, 72.75) * mm});
            skLineSegment(sketch, "E53.1.8.1", {"start": v(-54.44, 67.75) * mm, "end": v(-54.44, 77.75) * mm});
            skLineSegment(sketch, "E53.1.8.2", {"start": v(-54.44, 77.75) * mm, "end": v(-64.44, 77.75) * mm});
            skLineSegment(sketch, "E53.1.8.3", {"start": v(-54.44, 67.75) * mm, "end": v(-64.44, 67.75) * mm});
            skLineSegment(sketch, "E53.1.8.4", {"start": v(-64.44, 67.75) * mm, "end": v(-64.44, 77.75) * mm});
            skPoint(sketch, "E53.2.0.0", {"position": v(-44.44, -75.25) * mm});
            skLineSegment(sketch, "E53.2.0.1", {"start": v(-39.44, -80.25) * mm, "end": v(-39.44, -70.25) * mm});
            skLineSegment(sketch, "E53.2.0.2", {"start": v(-39.44, -70.25) * mm, "end": v(-49.44, -70.25) * mm});
            skLineSegment(sketch, "E53.2.0.3", {"start": v(-39.44, -80.25) * mm, "end": v(-49.44, -80.25) * mm});
            skLineSegment(sketch, "E53.2.0.4", {"start": v(-49.44, -80.25) * mm, "end": v(-49.44, -70.25) * mm});
            skPoint(sketch, "E53.2.1.0", {"position": v(-44.44, -56.75) * mm});
            skLineSegment(sketch, "E53.2.1.1", {"start": v(-39.44, -61.75) * mm, "end": v(-39.44, -51.75) * mm});
            skLineSegment(sketch, "E53.2.1.2", {"start": v(-39.44, -51.75) * mm, "end": v(-49.44, -51.75) * mm});
            skLineSegment(sketch, "E53.2.1.3", {"start": v(-39.44, -61.75) * mm, "end": v(-49.44, -61.75) * mm});
            skLineSegment(sketch, "E53.2.1.4", {"start": v(-49.44, -61.75) * mm, "end": v(-49.44, -51.75) * mm});
            skPoint(sketch, "E53.2.2.0", {"position": v(-44.44, -38.25) * mm});
            skLineSegment(sketch, "E53.2.2.1", {"start": v(-39.44, -43.25) * mm, "end": v(-39.44, -33.25) * mm});
            skLineSegment(sketch, "E53.2.2.2", {"start": v(-39.44, -33.25) * mm, "end": v(-49.44, -33.25) * mm});
            skLineSegment(sketch, "E53.2.2.3", {"start": v(-39.44, -43.25) * mm, "end": v(-49.44, -43.25) * mm});
            skLineSegment(sketch, "E53.2.2.4", {"start": v(-49.44, -43.25) * mm, "end": v(-49.44, -33.25) * mm});
            skPoint(sketch, "E53.2.3.0", {"position": v(-44.44, -19.75) * mm});
            skLineSegment(sketch, "E53.2.3.1", {"start": v(-39.44, -24.75) * mm, "end": v(-39.44, -14.75) * mm});
            skLineSegment(sketch, "E53.2.3.2", {"start": v(-39.44, -14.75) * mm, "end": v(-49.44, -14.75) * mm});
            skLineSegment(sketch, "E53.2.3.3", {"start": v(-39.44, -24.75) * mm, "end": v(-49.44, -24.75) * mm});
            skLineSegment(sketch, "E53.2.3.4", {"start": v(-49.44, -24.75) * mm, "end": v(-49.44, -14.75) * mm});
            skPoint(sketch, "E53.2.5.0", {"position": v(-44.44, 17.25) * mm});
            skLineSegment(sketch, "E53.2.5.1", {"start": v(-39.44, 12.25) * mm, "end": v(-39.44, 22.25) * mm});
            skLineSegment(sketch, "E53.2.5.2", {"start": v(-39.44, 22.25) * mm, "end": v(-49.44, 22.25) * mm});
            skLineSegment(sketch, "E53.2.5.3", {"start": v(-39.44, 12.25) * mm, "end": v(-49.44, 12.25) * mm});
            skLineSegment(sketch, "E53.2.5.4", {"start": v(-49.44, 12.25) * mm, "end": v(-49.44, 22.25) * mm});
            skPoint(sketch, "E53.2.6.0", {"position": v(-44.44, 35.75) * mm});
            skLineSegment(sketch, "E53.2.6.1", {"start": v(-39.44, 30.75) * mm, "end": v(-39.44, 40.75) * mm});
            skLineSegment(sketch, "E53.2.6.2", {"start": v(-39.44, 40.75) * mm, "end": v(-49.44, 40.75) * mm});
            skLineSegment(sketch, "E53.2.6.3", {"start": v(-39.44, 30.75) * mm, "end": v(-49.44, 30.75) * mm});
            skLineSegment(sketch, "E53.2.6.4", {"start": v(-49.44, 30.75) * mm, "end": v(-49.44, 40.75) * mm});
            skPoint(sketch, "E53.2.7.0", {"position": v(-44.44, 54.25) * mm});
            skLineSegment(sketch, "E53.2.7.1", {"start": v(-39.44, 49.25) * mm, "end": v(-39.44, 59.25) * mm});
            skLineSegment(sketch, "E53.2.7.2", {"start": v(-39.44, 59.25) * mm, "end": v(-49.44, 59.25) * mm});
            skLineSegment(sketch, "E53.2.7.3", {"start": v(-39.44, 49.25) * mm, "end": v(-49.44, 49.25) * mm});
            skLineSegment(sketch, "E53.2.7.4", {"start": v(-49.44, 49.25) * mm, "end": v(-49.44, 59.25) * mm});
            skPoint(sketch, "E53.2.8.0", {"position": v(-44.44, 72.75) * mm});
            skLineSegment(sketch, "E53.2.8.1", {"start": v(-39.44, 67.75) * mm, "end": v(-39.44, 77.75) * mm});
            skLineSegment(sketch, "E53.2.8.2", {"start": v(-39.44, 77.75) * mm, "end": v(-49.44, 77.75) * mm});
            skLineSegment(sketch, "E53.2.8.3", {"start": v(-39.44, 67.75) * mm, "end": v(-49.44, 67.75) * mm});
            skLineSegment(sketch, "E53.2.8.4", {"start": v(-49.44, 67.75) * mm, "end": v(-49.44, 77.75) * mm});
            skPoint(sketch, "E53.3.0.0", {"position": v(-29.44, -75.25) * mm});
            skLineSegment(sketch, "E53.3.0.1", {"start": v(-24.44, -80.25) * mm, "end": v(-24.44, -70.25) * mm});
            skLineSegment(sketch, "E53.3.0.2", {"start": v(-24.44, -70.25) * mm, "end": v(-34.44, -70.25) * mm});
            skLineSegment(sketch, "E53.3.0.3", {"start": v(-24.44, -80.25) * mm, "end": v(-34.44, -80.25) * mm});
            skLineSegment(sketch, "E53.3.0.4", {"start": v(-34.44, -80.25) * mm, "end": v(-34.44, -70.25) * mm});
            skPoint(sketch, "E53.3.1.0", {"position": v(-29.44, -56.75) * mm});
            skLineSegment(sketch, "E53.3.1.1", {"start": v(-24.44, -61.75) * mm, "end": v(-24.44, -51.75) * mm});
            skLineSegment(sketch, "E53.3.1.2", {"start": v(-24.44, -51.75) * mm, "end": v(-34.44, -51.75) * mm});
            skLineSegment(sketch, "E53.3.1.3", {"start": v(-24.44, -61.75) * mm, "end": v(-34.44, -61.75) * mm});
            skLineSegment(sketch, "E53.3.1.4", {"start": v(-34.44, -61.75) * mm, "end": v(-34.44, -51.75) * mm});
            skPoint(sketch, "E53.3.2.0", {"position": v(-29.44, -38.25) * mm});
            skLineSegment(sketch, "E53.3.2.1", {"start": v(-24.44, -43.25) * mm, "end": v(-24.44, -33.25) * mm});
            skLineSegment(sketch, "E53.3.2.2", {"start": v(-24.44, -33.25) * mm, "end": v(-34.44, -33.25) * mm});
            skLineSegment(sketch, "E53.3.2.3", {"start": v(-24.44, -43.25) * mm, "end": v(-34.44, -43.25) * mm});
            skLineSegment(sketch, "E53.3.2.4", {"start": v(-34.44, -43.25) * mm, "end": v(-34.44, -33.25) * mm});
            skPoint(sketch, "E53.3.3.0", {"position": v(-29.44, -19.75) * mm});
            skLineSegment(sketch, "E53.3.3.1", {"start": v(-24.44, -24.75) * mm, "end": v(-24.44, -14.75) * mm});
            skLineSegment(sketch, "E53.3.3.2", {"start": v(-24.44, -14.75) * mm, "end": v(-34.44, -14.75) * mm});
            skLineSegment(sketch, "E53.3.3.3", {"start": v(-24.44, -24.75) * mm, "end": v(-34.44, -24.75) * mm});
            skLineSegment(sketch, "E53.3.3.4", {"start": v(-34.44, -24.75) * mm, "end": v(-34.44, -14.75) * mm});
            skPoint(sketch, "E53.3.5.0", {"position": v(-29.44, 17.25) * mm});
            skLineSegment(sketch, "E53.3.5.1", {"start": v(-24.44, 12.25) * mm, "end": v(-24.44, 22.25) * mm});
            skLineSegment(sketch, "E53.3.5.2", {"start": v(-24.44, 22.25) * mm, "end": v(-34.44, 22.25) * mm});
            skLineSegment(sketch, "E53.3.5.3", {"start": v(-24.44, 12.25) * mm, "end": v(-34.44, 12.25) * mm});
            skLineSegment(sketch, "E53.3.5.4", {"start": v(-34.44, 12.25) * mm, "end": v(-34.44, 22.25) * mm});
            skPoint(sketch, "E53.3.6.0", {"position": v(-29.44, 35.75) * mm});
            skLineSegment(sketch, "E53.3.6.1", {"start": v(-24.44, 30.75) * mm, "end": v(-24.44, 40.75) * mm});
            skLineSegment(sketch, "E53.3.6.2", {"start": v(-24.44, 40.75) * mm, "end": v(-34.44, 40.75) * mm});
            skLineSegment(sketch, "E53.3.6.3", {"start": v(-24.44, 30.75) * mm, "end": v(-34.44, 30.75) * mm});
            skLineSegment(sketch, "E53.3.6.4", {"start": v(-34.44, 30.75) * mm, "end": v(-34.44, 40.75) * mm});
            skPoint(sketch, "E53.3.7.0", {"position": v(-29.44, 54.25) * mm});
            skLineSegment(sketch, "E53.3.7.1", {"start": v(-24.44, 49.25) * mm, "end": v(-24.44, 59.25) * mm});
            skLineSegment(sketch, "E53.3.7.2", {"start": v(-24.44, 59.25) * mm, "end": v(-34.44, 59.25) * mm});
            skLineSegment(sketch, "E53.3.7.3", {"start": v(-24.44, 49.25) * mm, "end": v(-34.44, 49.25) * mm});
            skLineSegment(sketch, "E53.3.7.4", {"start": v(-34.44, 49.25) * mm, "end": v(-34.44, 59.25) * mm});
            skPoint(sketch, "E53.3.8.0", {"position": v(-29.44, 72.75) * mm});
            skLineSegment(sketch, "E53.3.8.1", {"start": v(-24.44, 67.75) * mm, "end": v(-24.44, 77.75) * mm});
            skLineSegment(sketch, "E53.3.8.2", {"start": v(-24.44, 77.75) * mm, "end": v(-34.44, 77.75) * mm});
            skLineSegment(sketch, "E53.3.8.3", {"start": v(-24.44, 67.75) * mm, "end": v(-34.44, 67.75) * mm});
            skLineSegment(sketch, "E53.3.8.4", {"start": v(-34.44, 67.75) * mm, "end": v(-34.44, 77.75) * mm});
            skPoint(sketch, "E53.4.0.0", {"position": v(-14.44, -75.25) * mm});
            skLineSegment(sketch, "E53.4.0.1", {"start": v(-9.44, -80.25) * mm, "end": v(-9.44, -70.25) * mm});
            skLineSegment(sketch, "E53.4.0.2", {"start": v(-9.44, -70.25) * mm, "end": v(-19.44, -70.25) * mm});
            skLineSegment(sketch, "E53.4.0.3", {"start": v(-9.44, -80.25) * mm, "end": v(-19.44, -80.25) * mm});
            skLineSegment(sketch, "E53.4.0.4", {"start": v(-19.44, -80.25) * mm, "end": v(-19.44, -70.25) * mm});
            skPoint(sketch, "E53.4.1.0", {"position": v(-14.44, -56.75) * mm});
            skLineSegment(sketch, "E53.4.1.1", {"start": v(-9.44, -61.75) * mm, "end": v(-9.44, -51.75) * mm});
            skLineSegment(sketch, "E53.4.1.2", {"start": v(-9.44, -51.75) * mm, "end": v(-19.44, -51.75) * mm});
            skLineSegment(sketch, "E53.4.1.3", {"start": v(-9.44, -61.75) * mm, "end": v(-19.44, -61.75) * mm});
            skLineSegment(sketch, "E53.4.1.4", {"start": v(-19.44, -61.75) * mm, "end": v(-19.44, -51.75) * mm});
            skPoint(sketch, "E53.4.2.0", {"position": v(-14.44, -38.25) * mm});
            skLineSegment(sketch, "E53.4.2.1", {"start": v(-9.44, -43.25) * mm, "end": v(-9.44, -33.25) * mm});
            skLineSegment(sketch, "E53.4.2.2", {"start": v(-9.44, -33.25) * mm, "end": v(-19.44, -33.25) * mm});
            skLineSegment(sketch, "E53.4.2.3", {"start": v(-9.44, -43.25) * mm, "end": v(-19.44, -43.25) * mm});
            skLineSegment(sketch, "E53.4.2.4", {"start": v(-19.44, -43.25) * mm, "end": v(-19.44, -33.25) * mm});
            skPoint(sketch, "E53.4.3.0", {"position": v(-14.44, -19.75) * mm});
            skLineSegment(sketch, "E53.4.3.1", {"start": v(-9.44, -24.75) * mm, "end": v(-9.44, -14.75) * mm});
            skLineSegment(sketch, "E53.4.3.2", {"start": v(-9.44, -14.75) * mm, "end": v(-19.44, -14.75) * mm});
            skLineSegment(sketch, "E53.4.3.3", {"start": v(-9.44, -24.75) * mm, "end": v(-19.44, -24.75) * mm});
            skLineSegment(sketch, "E53.4.3.4", {"start": v(-19.44, -24.75) * mm, "end": v(-19.44, -14.75) * mm});
            skPoint(sketch, "E53.4.5.0", {"position": v(-14.44, 17.25) * mm});
            skLineSegment(sketch, "E53.4.5.1", {"start": v(-9.44, 12.25) * mm, "end": v(-9.44, 22.25) * mm});
            skLineSegment(sketch, "E53.4.5.2", {"start": v(-9.44, 22.25) * mm, "end": v(-19.44, 22.25) * mm});
            skLineSegment(sketch, "E53.4.5.3", {"start": v(-9.44, 12.25) * mm, "end": v(-19.44, 12.25) * mm});
            skLineSegment(sketch, "E53.4.5.4", {"start": v(-19.44, 12.25) * mm, "end": v(-19.44, 22.25) * mm});
            skPoint(sketch, "E53.4.6.0", {"position": v(-14.44, 35.75) * mm});
            skLineSegment(sketch, "E53.4.6.1", {"start": v(-9.44, 30.75) * mm, "end": v(-9.44, 40.75) * mm});
            skLineSegment(sketch, "E53.4.6.2", {"start": v(-9.44, 40.75) * mm, "end": v(-19.44, 40.75) * mm});
            skLineSegment(sketch, "E53.4.6.3", {"start": v(-9.44, 30.75) * mm, "end": v(-19.44, 30.75) * mm});
            skLineSegment(sketch, "E53.4.6.4", {"start": v(-19.44, 30.75) * mm, "end": v(-19.44, 40.75) * mm});
            skPoint(sketch, "E53.4.7.0", {"position": v(-14.44, 54.25) * mm});
            skLineSegment(sketch, "E53.4.7.1", {"start": v(-9.44, 49.25) * mm, "end": v(-9.44, 59.25) * mm});
            skLineSegment(sketch, "E53.4.7.2", {"start": v(-9.44, 59.25) * mm, "end": v(-19.44, 59.25) * mm});
            skLineSegment(sketch, "E53.4.7.3", {"start": v(-9.44, 49.25) * mm, "end": v(-19.44, 49.25) * mm});
            skLineSegment(sketch, "E53.4.7.4", {"start": v(-19.44, 49.25) * mm, "end": v(-19.44, 59.25) * mm});
            skPoint(sketch, "E53.4.8.0", {"position": v(-14.44, 72.75) * mm});
            skLineSegment(sketch, "E53.4.8.1", {"start": v(-9.44, 67.75) * mm, "end": v(-9.44, 77.75) * mm});
            skLineSegment(sketch, "E53.4.8.2", {"start": v(-9.44, 77.75) * mm, "end": v(-19.44, 77.75) * mm});
            skLineSegment(sketch, "E53.4.8.3", {"start": v(-9.44, 67.75) * mm, "end": v(-19.44, 67.75) * mm});
            skLineSegment(sketch, "E53.4.8.4", {"start": v(-19.44, 67.75) * mm, "end": v(-19.44, 77.75) * mm});
            skPoint(sketch, "E53.5.0.0", {"position": v(0.56, -75.25) * mm});
            skLineSegment(sketch, "E53.5.0.1", {"start": v(5.56, -80.25) * mm, "end": v(5.56, -70.25) * mm});
            skLineSegment(sketch, "E53.5.0.2", {"start": v(5.56, -70.25) * mm, "end": v(-4.44, -70.25) * mm});
            skLineSegment(sketch, "E53.5.0.3", {"start": v(5.56, -80.25) * mm, "end": v(-4.44, -80.25) * mm});
            skLineSegment(sketch, "E53.5.0.4", {"start": v(-4.44, -80.25) * mm, "end": v(-4.44, -70.25) * mm});
            skPoint(sketch, "E53.5.1.0", {"position": v(0.56, -56.75) * mm});
            skLineSegment(sketch, "E53.5.1.1", {"start": v(5.56, -61.75) * mm, "end": v(5.56, -51.75) * mm});
            skLineSegment(sketch, "E53.5.1.2", {"start": v(5.56, -51.75) * mm, "end": v(-4.44, -51.75) * mm});
            skLineSegment(sketch, "E53.5.1.3", {"start": v(5.56, -61.75) * mm, "end": v(-4.44, -61.75) * mm});
            skLineSegment(sketch, "E53.5.1.4", {"start": v(-4.44, -61.75) * mm, "end": v(-4.44, -51.75) * mm});
            skPoint(sketch, "E53.5.2.0", {"position": v(0.56, -38.25) * mm});
            skLineSegment(sketch, "E53.5.2.1", {"start": v(5.56, -43.25) * mm, "end": v(5.56, -33.25) * mm});
            skLineSegment(sketch, "E53.5.2.2", {"start": v(5.56, -33.25) * mm, "end": v(-4.44, -33.25) * mm});
            skLineSegment(sketch, "E53.5.2.3", {"start": v(5.56, -43.25) * mm, "end": v(-4.44, -43.25) * mm});
            skLineSegment(sketch, "E53.5.2.4", {"start": v(-4.44, -43.25) * mm, "end": v(-4.44, -33.25) * mm});
            skPoint(sketch, "E53.5.3.0", {"position": v(0.56, -19.75) * mm});
            skLineSegment(sketch, "E53.5.3.1", {"start": v(5.56, -24.75) * mm, "end": v(5.56, -14.75) * mm});
            skLineSegment(sketch, "E53.5.3.2", {"start": v(5.56, -14.75) * mm, "end": v(-4.44, -14.75) * mm});
            skLineSegment(sketch, "E53.5.3.3", {"start": v(5.56, -24.75) * mm, "end": v(-4.44, -24.75) * mm});
            skLineSegment(sketch, "E53.5.3.4", {"start": v(-4.44, -24.75) * mm, "end": v(-4.44, -14.75) * mm});
            skPoint(sketch, "E53.5.5.0", {"position": v(0.56, 17.25) * mm});
            skLineSegment(sketch, "E53.5.5.1", {"start": v(5.56, 12.25) * mm, "end": v(5.56, 22.25) * mm});
            skLineSegment(sketch, "E53.5.5.2", {"start": v(5.56, 22.25) * mm, "end": v(-4.44, 22.25) * mm});
            skLineSegment(sketch, "E53.5.5.3", {"start": v(5.56, 12.25) * mm, "end": v(-4.44, 12.25) * mm});
            skLineSegment(sketch, "E53.5.5.4", {"start": v(-4.44, 12.25) * mm, "end": v(-4.44, 22.25) * mm});
            skPoint(sketch, "E53.5.6.0", {"position": v(0.56, 35.75) * mm});
            skLineSegment(sketch, "E53.5.6.1", {"start": v(5.56, 30.75) * mm, "end": v(5.56, 40.75) * mm});
            skLineSegment(sketch, "E53.5.6.2", {"start": v(5.56, 40.75) * mm, "end": v(-4.44, 40.75) * mm});
            skLineSegment(sketch, "E53.5.6.3", {"start": v(5.56, 30.75) * mm, "end": v(-4.44, 30.75) * mm});
            skLineSegment(sketch, "E53.5.6.4", {"start": v(-4.44, 30.75) * mm, "end": v(-4.44, 40.75) * mm});
            skPoint(sketch, "E53.5.7.0", {"position": v(0.56, 54.25) * mm});
            skLineSegment(sketch, "E53.5.7.1", {"start": v(5.56, 49.25) * mm, "end": v(5.56, 59.25) * mm});
            skLineSegment(sketch, "E53.5.7.2", {"start": v(5.56, 59.25) * mm, "end": v(-4.44, 59.25) * mm});
            skLineSegment(sketch, "E53.5.7.3", {"start": v(5.56, 49.25) * mm, "end": v(-4.44, 49.25) * mm});
            skLineSegment(sketch, "E53.5.7.4", {"start": v(-4.44, 49.25) * mm, "end": v(-4.44, 59.25) * mm});
            skPoint(sketch, "E53.5.8.0", {"position": v(0.56, 72.75) * mm});
            skLineSegment(sketch, "E53.5.8.1", {"start": v(5.56, 67.75) * mm, "end": v(5.56, 77.75) * mm});
            skLineSegment(sketch, "E53.5.8.2", {"start": v(5.56, 77.75) * mm, "end": v(-4.44, 77.75) * mm});
            skLineSegment(sketch, "E53.5.8.3", {"start": v(5.56, 67.75) * mm, "end": v(-4.44, 67.75) * mm});
            skLineSegment(sketch, "E53.5.8.4", {"start": v(-4.44, 67.75) * mm, "end": v(-4.44, 77.75) * mm});
            skPoint(sketch, "E53.6.0.0", {"position": v(15.56, -75.25) * mm});
            skLineSegment(sketch, "E53.6.0.1", {"start": v(20.56, -80.25) * mm, "end": v(20.56, -70.25) * mm});
            skLineSegment(sketch, "E53.6.0.2", {"start": v(20.56, -70.25) * mm, "end": v(10.56, -70.25) * mm});
            skLineSegment(sketch, "E53.6.0.3", {"start": v(20.56, -80.25) * mm, "end": v(10.56, -80.25) * mm});
            skLineSegment(sketch, "E53.6.0.4", {"start": v(10.56, -80.25) * mm, "end": v(10.56, -70.25) * mm});
            skPoint(sketch, "E53.6.1.0", {"position": v(15.56, -56.75) * mm});
            skLineSegment(sketch, "E53.6.1.1", {"start": v(20.56, -61.75) * mm, "end": v(20.56, -51.75) * mm});
            skLineSegment(sketch, "E53.6.1.2", {"start": v(20.56, -51.75) * mm, "end": v(10.56, -51.75) * mm});
            skLineSegment(sketch, "E53.6.1.3", {"start": v(20.56, -61.75) * mm, "end": v(10.56, -61.75) * mm});
            skLineSegment(sketch, "E53.6.1.4", {"start": v(10.56, -61.75) * mm, "end": v(10.56, -51.75) * mm});
            skPoint(sketch, "E53.6.2.0", {"position": v(15.56, -38.25) * mm});
            skLineSegment(sketch, "E53.6.2.1", {"start": v(20.56, -43.25) * mm, "end": v(20.56, -33.25) * mm});
            skLineSegment(sketch, "E53.6.2.2", {"start": v(20.56, -33.25) * mm, "end": v(10.56, -33.25) * mm});
            skLineSegment(sketch, "E53.6.2.3", {"start": v(20.56, -43.25) * mm, "end": v(10.56, -43.25) * mm});
            skLineSegment(sketch, "E53.6.2.4", {"start": v(10.56, -43.25) * mm, "end": v(10.56, -33.25) * mm});
            skPoint(sketch, "E53.6.3.0", {"position": v(15.56, -19.75) * mm});
            skLineSegment(sketch, "E53.6.3.1", {"start": v(20.56, -24.75) * mm, "end": v(20.56, -14.75) * mm});
            skLineSegment(sketch, "E53.6.3.2", {"start": v(20.56, -14.75) * mm, "end": v(10.56, -14.75) * mm});
            skLineSegment(sketch, "E53.6.3.3", {"start": v(20.56, -24.75) * mm, "end": v(10.56, -24.75) * mm});
            skLineSegment(sketch, "E53.6.3.4", {"start": v(10.56, -24.75) * mm, "end": v(10.56, -14.75) * mm});
            skPoint(sketch, "E53.6.5.0", {"position": v(15.56, 17.25) * mm});
            skLineSegment(sketch, "E53.6.5.1", {"start": v(20.56, 12.25) * mm, "end": v(20.56, 22.25) * mm});
            skLineSegment(sketch, "E53.6.5.2", {"start": v(20.56, 22.25) * mm, "end": v(10.56, 22.25) * mm});
            skLineSegment(sketch, "E53.6.5.3", {"start": v(20.56, 12.25) * mm, "end": v(10.56, 12.25) * mm});
            skLineSegment(sketch, "E53.6.5.4", {"start": v(10.56, 12.25) * mm, "end": v(10.56, 22.25) * mm});
            skPoint(sketch, "E53.6.6.0", {"position": v(15.56, 35.75) * mm});
            skLineSegment(sketch, "E53.6.6.1", {"start": v(20.56, 30.75) * mm, "end": v(20.56, 40.75) * mm});
            skLineSegment(sketch, "E53.6.6.2", {"start": v(20.56, 40.75) * mm, "end": v(10.56, 40.75) * mm});
            skLineSegment(sketch, "E53.6.6.3", {"start": v(20.56, 30.75) * mm, "end": v(10.56, 30.75) * mm});
            skLineSegment(sketch, "E53.6.6.4", {"start": v(10.56, 30.75) * mm, "end": v(10.56, 40.75) * mm});
            skPoint(sketch, "E53.6.7.0", {"position": v(15.56, 54.25) * mm});
            skLineSegment(sketch, "E53.6.7.1", {"start": v(20.56, 49.25) * mm, "end": v(20.56, 59.25) * mm});
            skLineSegment(sketch, "E53.6.7.2", {"start": v(20.56, 59.25) * mm, "end": v(10.56, 59.25) * mm});
            skLineSegment(sketch, "E53.6.7.3", {"start": v(20.56, 49.25) * mm, "end": v(10.56, 49.25) * mm});
            skLineSegment(sketch, "E53.6.7.4", {"start": v(10.56, 49.25) * mm, "end": v(10.56, 59.25) * mm});
            skPoint(sketch, "E53.6.8.0", {"position": v(15.56, 72.75) * mm});
            skLineSegment(sketch, "E53.6.8.1", {"start": v(20.56, 67.75) * mm, "end": v(20.56, 77.75) * mm});
            skLineSegment(sketch, "E53.6.8.2", {"start": v(20.56, 77.75) * mm, "end": v(10.56, 77.75) * mm});
            skLineSegment(sketch, "E53.6.8.3", {"start": v(20.56, 67.75) * mm, "end": v(10.56, 67.75) * mm});
            skLineSegment(sketch, "E53.6.8.4", {"start": v(10.56, 67.75) * mm, "end": v(10.56, 77.75) * mm});
            skPoint(sketch, "E53.7.0.0", {"position": v(30.56, -75.25) * mm});
            skLineSegment(sketch, "E53.7.0.1", {"start": v(35.56, -80.25) * mm, "end": v(35.56, -70.25) * mm});
            skLineSegment(sketch, "E53.7.0.2", {"start": v(35.56, -70.25) * mm, "end": v(25.56, -70.25) * mm});
            skLineSegment(sketch, "E53.7.0.3", {"start": v(35.56, -80.25) * mm, "end": v(25.56, -80.25) * mm});
            skLineSegment(sketch, "E53.7.0.4", {"start": v(25.56, -80.25) * mm, "end": v(25.56, -70.25) * mm});
            skPoint(sketch, "E53.7.1.0", {"position": v(30.56, -56.75) * mm});
            skLineSegment(sketch, "E53.7.1.1", {"start": v(35.56, -61.75) * mm, "end": v(35.56, -51.75) * mm});
            skLineSegment(sketch, "E53.7.1.2", {"start": v(35.56, -51.75) * mm, "end": v(25.56, -51.75) * mm});
            skLineSegment(sketch, "E53.7.1.3", {"start": v(35.56, -61.75) * mm, "end": v(25.56, -61.75) * mm});
            skLineSegment(sketch, "E53.7.1.4", {"start": v(25.56, -61.75) * mm, "end": v(25.56, -51.75) * mm});
            skPoint(sketch, "E53.7.2.0", {"position": v(30.56, -38.25) * mm});
            skLineSegment(sketch, "E53.7.2.1", {"start": v(35.56, -43.25) * mm, "end": v(35.56, -33.25) * mm});
            skLineSegment(sketch, "E53.7.2.2", {"start": v(35.56, -33.25) * mm, "end": v(25.56, -33.25) * mm});
            skLineSegment(sketch, "E53.7.2.3", {"start": v(35.56, -43.25) * mm, "end": v(25.56, -43.25) * mm});
            skLineSegment(sketch, "E53.7.2.4", {"start": v(25.56, -43.25) * mm, "end": v(25.56, -33.25) * mm});
            skPoint(sketch, "E53.7.3.0", {"position": v(30.56, -19.75) * mm});
            skLineSegment(sketch, "E53.7.3.1", {"start": v(35.56, -24.75) * mm, "end": v(35.56, -14.75) * mm});
            skLineSegment(sketch, "E53.7.3.2", {"start": v(35.56, -14.75) * mm, "end": v(25.56, -14.75) * mm});
            skLineSegment(sketch, "E53.7.3.3", {"start": v(35.56, -24.75) * mm, "end": v(25.56, -24.75) * mm});
            skLineSegment(sketch, "E53.7.3.4", {"start": v(25.56, -24.75) * mm, "end": v(25.56, -14.75) * mm});
            skPoint(sketch, "E53.7.5.0", {"position": v(30.56, 17.25) * mm});
            skLineSegment(sketch, "E53.7.5.1", {"start": v(35.56, 12.25) * mm, "end": v(35.56, 22.25) * mm});
            skLineSegment(sketch, "E53.7.5.2", {"start": v(35.56, 22.25) * mm, "end": v(25.56, 22.25) * mm});
            skLineSegment(sketch, "E53.7.5.3", {"start": v(35.56, 12.25) * mm, "end": v(25.56, 12.25) * mm});
            skLineSegment(sketch, "E53.7.5.4", {"start": v(25.56, 12.25) * mm, "end": v(25.56, 22.25) * mm});
            skPoint(sketch, "E53.7.6.0", {"position": v(30.56, 35.75) * mm});
            skLineSegment(sketch, "E53.7.6.1", {"start": v(35.56, 30.75) * mm, "end": v(35.56, 40.75) * mm});
            skLineSegment(sketch, "E53.7.6.2", {"start": v(35.56, 40.75) * mm, "end": v(25.56, 40.75) * mm});
            skLineSegment(sketch, "E53.7.6.3", {"start": v(35.56, 30.75) * mm, "end": v(25.56, 30.75) * mm});
            skLineSegment(sketch, "E53.7.6.4", {"start": v(25.56, 30.75) * mm, "end": v(25.56, 40.75) * mm});
            skPoint(sketch, "E53.7.7.0", {"position": v(30.56, 54.25) * mm});
            skLineSegment(sketch, "E53.7.7.1", {"start": v(35.56, 49.25) * mm, "end": v(35.56, 59.25) * mm});
            skLineSegment(sketch, "E53.7.7.2", {"start": v(35.56, 59.25) * mm, "end": v(25.56, 59.25) * mm});
            skLineSegment(sketch, "E53.7.7.3", {"start": v(35.56, 49.25) * mm, "end": v(25.56, 49.25) * mm});
            skLineSegment(sketch, "E53.7.7.4", {"start": v(25.56, 49.25) * mm, "end": v(25.56, 59.25) * mm});
            skPoint(sketch, "E53.7.8.0", {"position": v(30.56, 72.75) * mm});
            skLineSegment(sketch, "E53.7.8.1", {"start": v(35.56, 67.75) * mm, "end": v(35.56, 77.75) * mm});
            skLineSegment(sketch, "E53.7.8.2", {"start": v(35.56, 77.75) * mm, "end": v(25.56, 77.75) * mm});
            skLineSegment(sketch, "E53.7.8.3", {"start": v(35.56, 67.75) * mm, "end": v(25.56, 67.75) * mm});
            skLineSegment(sketch, "E53.7.8.4", {"start": v(25.56, 67.75) * mm, "end": v(25.56, 77.75) * mm});
            skPoint(sketch, "E53.8.0.0", {"position": v(45.56, -75.25) * mm});
            skLineSegment(sketch, "E53.8.0.1", {"start": v(50.56, -80.25) * mm, "end": v(50.56, -70.25) * mm});
            skLineSegment(sketch, "E53.8.0.2", {"start": v(50.56, -70.25) * mm, "end": v(40.56, -70.25) * mm});
            skLineSegment(sketch, "E53.8.0.3", {"start": v(50.56, -80.25) * mm, "end": v(40.56, -80.25) * mm});
            skLineSegment(sketch, "E53.8.0.4", {"start": v(40.56, -80.25) * mm, "end": v(40.56, -70.25) * mm});
            skPoint(sketch, "E53.8.1.0", {"position": v(45.56, -56.75) * mm});
            skLineSegment(sketch, "E53.8.1.1", {"start": v(50.56, -61.75) * mm, "end": v(50.56, -51.75) * mm});
            skLineSegment(sketch, "E53.8.1.2", {"start": v(50.56, -51.75) * mm, "end": v(40.56, -51.75) * mm});
            skLineSegment(sketch, "E53.8.1.3", {"start": v(50.56, -61.75) * mm, "end": v(40.56, -61.75) * mm});
            skLineSegment(sketch, "E53.8.1.4", {"start": v(40.56, -61.75) * mm, "end": v(40.56, -51.75) * mm});
            skPoint(sketch, "E53.8.2.0", {"position": v(45.56, -38.25) * mm});
            skLineSegment(sketch, "E53.8.2.1", {"start": v(50.56, -43.25) * mm, "end": v(50.56, -33.25) * mm});
            skLineSegment(sketch, "E53.8.2.2", {"start": v(50.56, -33.25) * mm, "end": v(40.56, -33.25) * mm});
            skLineSegment(sketch, "E53.8.2.3", {"start": v(50.56, -43.25) * mm, "end": v(40.56, -43.25) * mm});
            skLineSegment(sketch, "E53.8.2.4", {"start": v(40.56, -43.25) * mm, "end": v(40.56, -33.25) * mm});
            skPoint(sketch, "E53.8.3.0", {"position": v(45.56, -19.75) * mm});
            skLineSegment(sketch, "E53.8.3.1", {"start": v(50.56, -24.75) * mm, "end": v(50.56, -14.75) * mm});
            skLineSegment(sketch, "E53.8.3.2", {"start": v(50.56, -14.75) * mm, "end": v(40.56, -14.75) * mm});
            skLineSegment(sketch, "E53.8.3.3", {"start": v(50.56, -24.75) * mm, "end": v(40.56, -24.75) * mm});
            skLineSegment(sketch, "E53.8.3.4", {"start": v(40.56, -24.75) * mm, "end": v(40.56, -14.75) * mm});
            skPoint(sketch, "E53.8.5.0", {"position": v(45.56, 17.25) * mm});
            skLineSegment(sketch, "E53.8.5.1", {"start": v(50.56, 12.25) * mm, "end": v(50.56, 22.25) * mm});
            skLineSegment(sketch, "E53.8.5.2", {"start": v(50.56, 22.25) * mm, "end": v(40.56, 22.25) * mm});
            skLineSegment(sketch, "E53.8.5.3", {"start": v(50.56, 12.25) * mm, "end": v(40.56, 12.25) * mm});
            skLineSegment(sketch, "E53.8.5.4", {"start": v(40.56, 12.25) * mm, "end": v(40.56, 22.25) * mm});
            skPoint(sketch, "E53.8.6.0", {"position": v(45.56, 35.75) * mm});
            skLineSegment(sketch, "E53.8.6.1", {"start": v(50.56, 30.75) * mm, "end": v(50.56, 40.75) * mm});
            skLineSegment(sketch, "E53.8.6.2", {"start": v(50.56, 40.75) * mm, "end": v(40.56, 40.75) * mm});
            skLineSegment(sketch, "E53.8.6.3", {"start": v(50.56, 30.75) * mm, "end": v(40.56, 30.75) * mm});
            skLineSegment(sketch, "E53.8.6.4", {"start": v(40.56, 30.75) * mm, "end": v(40.56, 40.75) * mm});
            skPoint(sketch, "E53.8.7.0", {"position": v(45.56, 54.25) * mm});
            skLineSegment(sketch, "E53.8.7.1", {"start": v(50.56, 49.25) * mm, "end": v(50.56, 59.25) * mm});
            skLineSegment(sketch, "E53.8.7.2", {"start": v(50.56, 59.25) * mm, "end": v(40.56, 59.25) * mm});
            skLineSegment(sketch, "E53.8.7.3", {"start": v(50.56, 49.25) * mm, "end": v(40.56, 49.25) * mm});
            skLineSegment(sketch, "E53.8.7.4", {"start": v(40.56, 49.25) * mm, "end": v(40.56, 59.25) * mm});
            skPoint(sketch, "E53.8.8.0", {"position": v(45.56, 72.75) * mm});
            skLineSegment(sketch, "E53.8.8.1", {"start": v(50.56, 67.75) * mm, "end": v(50.56, 77.75) * mm});
            skLineSegment(sketch, "E53.8.8.2", {"start": v(50.56, 77.75) * mm, "end": v(40.56, 77.75) * mm});
            skLineSegment(sketch, "E53.8.8.3", {"start": v(50.56, 67.75) * mm, "end": v(40.56, 67.75) * mm});
            skLineSegment(sketch, "E53.8.8.4", {"start": v(40.56, 67.75) * mm, "end": v(40.56, 77.75) * mm});
            skPoint(sketch, "E53.9.0.0", {"position": v(60.56, -75.25) * mm});
            skLineSegment(sketch, "E53.9.0.1", {"start": v(65.56, -80.25) * mm, "end": v(65.56, -70.25) * mm});
            skLineSegment(sketch, "E53.9.0.2", {"start": v(65.56, -70.25) * mm, "end": v(55.56, -70.25) * mm});
            skLineSegment(sketch, "E53.9.0.3", {"start": v(65.56, -80.25) * mm, "end": v(55.56, -80.25) * mm});
            skLineSegment(sketch, "E53.9.0.4", {"start": v(55.56, -80.25) * mm, "end": v(55.56, -70.25) * mm});
            skPoint(sketch, "E53.9.1.0", {"position": v(60.56, -56.75) * mm});
            skLineSegment(sketch, "E53.9.1.1", {"start": v(65.56, -61.75) * mm, "end": v(65.56, -51.75) * mm});
            skLineSegment(sketch, "E53.9.1.2", {"start": v(65.56, -51.75) * mm, "end": v(55.56, -51.75) * mm});
            skLineSegment(sketch, "E53.9.1.3", {"start": v(65.56, -61.75) * mm, "end": v(55.56, -61.75) * mm});
            skLineSegment(sketch, "E53.9.1.4", {"start": v(55.56, -61.75) * mm, "end": v(55.56, -51.75) * mm});
            skPoint(sketch, "E53.9.2.0", {"position": v(60.56, -38.25) * mm});
            skLineSegment(sketch, "E53.9.2.1", {"start": v(65.56, -43.25) * mm, "end": v(65.56, -33.25) * mm});
            skLineSegment(sketch, "E53.9.2.2", {"start": v(65.56, -33.25) * mm, "end": v(55.56, -33.25) * mm});
            skLineSegment(sketch, "E53.9.2.3", {"start": v(65.56, -43.25) * mm, "end": v(55.56, -43.25) * mm});
            skLineSegment(sketch, "E53.9.2.4", {"start": v(55.56, -43.25) * mm, "end": v(55.56, -33.25) * mm});
            skPoint(sketch, "E53.9.3.0", {"position": v(60.56, -19.75) * mm});
            skLineSegment(sketch, "E53.9.3.1", {"start": v(65.56, -24.75) * mm, "end": v(65.56, -14.75) * mm});
            skLineSegment(sketch, "E53.9.3.2", {"start": v(65.56, -14.75) * mm, "end": v(55.56, -14.75) * mm});
            skLineSegment(sketch, "E53.9.3.3", {"start": v(65.56, -24.75) * mm, "end": v(55.56, -24.75) * mm});
            skLineSegment(sketch, "E53.9.3.4", {"start": v(55.56, -24.75) * mm, "end": v(55.56, -14.75) * mm});
            skPoint(sketch, "E53.9.5.0", {"position": v(60.56, 17.25) * mm});
            skLineSegment(sketch, "E53.9.5.1", {"start": v(65.56, 12.25) * mm, "end": v(65.56, 22.25) * mm});
            skLineSegment(sketch, "E53.9.5.2", {"start": v(65.56, 22.25) * mm, "end": v(55.56, 22.25) * mm});
            skLineSegment(sketch, "E53.9.5.3", {"start": v(65.56, 12.25) * mm, "end": v(55.56, 12.25) * mm});
            skLineSegment(sketch, "E53.9.5.4", {"start": v(55.56, 12.25) * mm, "end": v(55.56, 22.25) * mm});
            skPoint(sketch, "E53.9.6.0", {"position": v(60.56, 35.75) * mm});
            skLineSegment(sketch, "E53.9.6.1", {"start": v(65.56, 30.75) * mm, "end": v(65.56, 40.75) * mm});
            skLineSegment(sketch, "E53.9.6.2", {"start": v(65.56, 40.75) * mm, "end": v(55.56, 40.75) * mm});
            skLineSegment(sketch, "E53.9.6.3", {"start": v(65.56, 30.75) * mm, "end": v(55.56, 30.75) * mm});
            skLineSegment(sketch, "E53.9.6.4", {"start": v(55.56, 30.75) * mm, "end": v(55.56, 40.75) * mm});
            skPoint(sketch, "E53.9.7.0", {"position": v(60.56, 54.25) * mm});
            skLineSegment(sketch, "E53.9.7.1", {"start": v(65.56, 49.25) * mm, "end": v(65.56, 59.25) * mm});
            skLineSegment(sketch, "E53.9.7.2", {"start": v(65.56, 59.25) * mm, "end": v(55.56, 59.25) * mm});
            skLineSegment(sketch, "E53.9.7.3", {"start": v(65.56, 49.25) * mm, "end": v(55.56, 49.25) * mm});
            skLineSegment(sketch, "E53.9.7.4", {"start": v(55.56, 49.25) * mm, "end": v(55.56, 59.25) * mm});
            skPoint(sketch, "E53.9.8.0", {"position": v(60.56, 72.75) * mm});
            skLineSegment(sketch, "E53.9.8.1", {"start": v(65.56, 67.75) * mm, "end": v(65.56, 77.75) * mm});
            skLineSegment(sketch, "E53.9.8.2", {"start": v(65.56, 77.75) * mm, "end": v(55.56, 77.75) * mm});
            skLineSegment(sketch, "E53.9.8.3", {"start": v(65.56, 67.75) * mm, "end": v(55.56, 67.75) * mm});
            skLineSegment(sketch, "E53.9.8.4", {"start": v(55.56, 67.75) * mm, "end": v(55.56, 77.75) * mm});
            skPoint(sketch, "E53.10.0.0", {"position": v(75.56, -75.25) * mm});
            skLineSegment(sketch, "E53.10.0.1", {"start": v(80.56, -80.25) * mm, "end": v(80.56, -70.25) * mm});
            skLineSegment(sketch, "E53.10.0.2", {"start": v(80.56, -70.25) * mm, "end": v(70.56, -70.25) * mm});
            skLineSegment(sketch, "E53.10.0.3", {"start": v(80.56, -80.25) * mm, "end": v(70.56, -80.25) * mm});
            skLineSegment(sketch, "E53.10.0.4", {"start": v(70.56, -80.25) * mm, "end": v(70.56, -70.25) * mm});
            skPoint(sketch, "E53.10.1.0", {"position": v(75.56, -56.75) * mm});
            skLineSegment(sketch, "E53.10.1.1", {"start": v(80.56, -61.75) * mm, "end": v(80.56, -51.75) * mm});
            skLineSegment(sketch, "E53.10.1.2", {"start": v(80.56, -51.75) * mm, "end": v(70.56, -51.75) * mm});
            skLineSegment(sketch, "E53.10.1.3", {"start": v(80.56, -61.75) * mm, "end": v(70.56, -61.75) * mm});
            skLineSegment(sketch, "E53.10.1.4", {"start": v(70.56, -61.75) * mm, "end": v(70.56, -51.75) * mm});
            skPoint(sketch, "E53.10.2.0", {"position": v(75.56, -38.25) * mm});
            skLineSegment(sketch, "E53.10.2.1", {"start": v(80.56, -43.25) * mm, "end": v(80.56, -33.25) * mm});
            skLineSegment(sketch, "E53.10.2.2", {"start": v(80.56, -33.25) * mm, "end": v(70.56, -33.25) * mm});
            skLineSegment(sketch, "E53.10.2.3", {"start": v(80.56, -43.25) * mm, "end": v(70.56, -43.25) * mm});
            skLineSegment(sketch, "E53.10.2.4", {"start": v(70.56, -43.25) * mm, "end": v(70.56, -33.25) * mm});
            skPoint(sketch, "E53.10.3.0", {"position": v(75.56, -19.75) * mm});
            skLineSegment(sketch, "E53.10.3.1", {"start": v(80.56, -24.75) * mm, "end": v(80.56, -14.75) * mm});
            skLineSegment(sketch, "E53.10.3.2", {"start": v(80.56, -14.75) * mm, "end": v(70.56, -14.75) * mm});
            skLineSegment(sketch, "E53.10.3.3", {"start": v(80.56, -24.75) * mm, "end": v(70.56, -24.75) * mm});
            skLineSegment(sketch, "E53.10.3.4", {"start": v(70.56, -24.75) * mm, "end": v(70.56, -14.75) * mm});
            skPoint(sketch, "E53.10.5.0", {"position": v(75.56, 17.25) * mm});
            skLineSegment(sketch, "E53.10.5.1", {"start": v(80.56, 12.25) * mm, "end": v(80.56, 22.25) * mm});
            skLineSegment(sketch, "E53.10.5.2", {"start": v(80.56, 22.25) * mm, "end": v(70.56, 22.25) * mm});
            skLineSegment(sketch, "E53.10.5.3", {"start": v(80.56, 12.25) * mm, "end": v(70.56, 12.25) * mm});
            skLineSegment(sketch, "E53.10.5.4", {"start": v(70.56, 12.25) * mm, "end": v(70.56, 22.25) * mm});
            skPoint(sketch, "E53.10.6.0", {"position": v(75.56, 35.75) * mm});
            skLineSegment(sketch, "E53.10.6.1", {"start": v(80.56, 30.75) * mm, "end": v(80.56, 40.75) * mm});
            skLineSegment(sketch, "E53.10.6.2", {"start": v(80.56, 40.75) * mm, "end": v(70.56, 40.75) * mm});
            skLineSegment(sketch, "E53.10.6.3", {"start": v(80.56, 30.75) * mm, "end": v(70.56, 30.75) * mm});
            skLineSegment(sketch, "E53.10.6.4", {"start": v(70.56, 30.75) * mm, "end": v(70.56, 40.75) * mm});
            skPoint(sketch, "E53.10.7.0", {"position": v(75.56, 54.25) * mm});
            skLineSegment(sketch, "E53.10.7.1", {"start": v(80.56, 49.25) * mm, "end": v(80.56, 59.25) * mm});
            skLineSegment(sketch, "E53.10.7.2", {"start": v(80.56, 59.25) * mm, "end": v(70.56, 59.25) * mm});
            skLineSegment(sketch, "E53.10.7.3", {"start": v(80.56, 49.25) * mm, "end": v(70.56, 49.25) * mm});
            skLineSegment(sketch, "E53.10.7.4", {"start": v(70.56, 49.25) * mm, "end": v(70.56, 59.25) * mm});
            skPoint(sketch, "E53.10.8.0", {"position": v(75.56, 72.75) * mm});
            skLineSegment(sketch, "E53.10.8.1", {"start": v(80.56, 67.75) * mm, "end": v(80.56, 77.75) * mm});
            skLineSegment(sketch, "E53.10.8.2", {"start": v(80.56, 77.75) * mm, "end": v(70.56, 77.75) * mm});
            skLineSegment(sketch, "E53.10.8.3", {"start": v(80.56, 67.75) * mm, "end": v(70.56, 67.75) * mm});
            skLineSegment(sketch, "E53.10.8.4", {"start": v(70.56, 67.75) * mm, "end": v(70.56, 77.75) * mm});
            skLineSegment(sketch, "E53.direction1", {"start": v(-79.44, -80.25) * mm, "end": v(-64.44, -80.25) * mm, "construction": true});
            skLineSegment(sketch, "E53.direction2", {"start": v(-79.44, -80.25) * mm, "end": v(-79.44, -61.75) * mm, "construction": true});
            skSolve(sketch);
        }
        {
            var Q0;
            Q0=qSketchRegion(id+"F24",true);
            extrude(context, id + "F25", {"entities" : qUnion([Q0]), "operationType" : NewBodyOperationType.REMOVE, "endBound" : BoundingType.SYMMETRIC, "oppositeDirection" : true, "depth" : 300 * mm, "offsetDistance" : 25 * mm});
        }
        {
            var Q0;
            Q0=makeQuery(id+"F2.imprint","IMPRINT",FACE,{"disambiguationData":[TD([[makeQuery(id+"F2.imprint","IMPRINT",EDGE,{"derivedFrom":sQuery(id+"F2.wireOp",EDGE,"E1.bottom")}),-1.0]])]});
            var sketch = newSketch(context, id + "F26", { "sketchPlane" : qUnion([Q0])});
            skLineSegment(sketch, "E54", {"start": v(-117.68, 0) * mm, "end": v(121.84, 0) * mm, "construction": true});
            skLineSegment(sketch, "E55.bottom", {"start": v(-107.47, -2) * mm, "end": v(-112.47, -2) * mm, "construction": true});
            skLineSegment(sketch, "E55.top", {"start": v(-107.47, 2) * mm, "end": v(-112.47, 2) * mm, "construction": true});
            skLineSegment(sketch, "E55.left", {"start": v(-107.47, -2) * mm, "end": v(-107.47, 2) * mm, "construction": true});
            skLineSegment(sketch, "E55.right", {"start": v(-112.47, -2) * mm, "end": v(-112.47, 2) * mm, "construction": true});
            skPoint(sketch, "E55.middle", {"position": v(-109.97, 0) * mm});
            skLineSegment(sketch, "E56.bottom", {"start": v(112.53, -2) * mm, "end": v(107.53, -2) * mm});
            skLineSegment(sketch, "E56.top", {"start": v(112.53, 2) * mm, "end": v(107.53, 2) * mm});
            skLineSegment(sketch, "E56.left", {"start": v(112.53, -2) * mm, "end": v(112.53, 2) * mm});
            skLineSegment(sketch, "E56.right", {"start": v(107.53, -2) * mm, "end": v(107.53, 2) * mm});
            skPoint(sketch, "E56.middle", {"position": v(110.03, 0) * mm});
            skSolve(sketch);
        }
        {
            var Q0;
            Q0=qSketchRegion(id+"F26",true);
            extrude(context, id + "F27", {"entities" : qUnion([Q0]), "operationType" : NewBodyOperationType.ADD, "oppositeDirection" : true, "depth" : 10 * mm, "offsetDistance" : 25 * mm});
        }
        {
            var Q0;
            Q0=makeQuery(id+"F2.imprint","IMPRINT",FACE,{"disambiguationData":[TD([[makeQuery(id+"F2.imprint","IMPRINT",EDGE,{"derivedFrom":sQuery(id+"F2.wireOp",EDGE,"E1.bottom")}),1.0]])]});
            var sketch = newSketch(context, id + "F28", { "sketchPlane" : qUnion([Q0])});
            skCircle(sketch, "E57", {"center": v(110.08, 0) * mm, "radius": 1.45 * mm});
            skSolve(sketch);
        }
        {
            var Q0;
            Q0=qSketchRegion(id+"F28",true);
            extrude(context, id + "F29", {"entities" : qUnion([Q0]), "operationType" : NewBodyOperationType.REMOVE, "oppositeDirection" : true, "depth" : 10 * mm, "offsetDistance" : 25 * mm});
        }
        {
            var Q0;
            Q0=makeQuery(id+"F2.imprint","IMPRINT",FACE,{"disambiguationData":[TD([[makeQuery(id+"F2.imprint","IMPRINT",EDGE,{"derivedFrom":sQuery(id+"F2.wireOp",EDGE,"E1.bottom")}),1.0]])]});
            var sketch = newSketch(context, id + "F30", { "sketchPlane" : qUnion([Q0])});
            skLineSegment(sketch, "E58.bottom", {"start": v(-107.3, -2.53) * mm, "end": v(-112.48, -2.53) * mm});
            skLineSegment(sketch, "E58.top", {"start": v(-107.3, 2.53) * mm, "end": v(-112.48, 2.53) * mm});
            skLineSegment(sketch, "E58.left", {"start": v(-107.3, -2.53) * mm, "end": v(-107.3, 2.53) * mm});
            skLineSegment(sketch, "E58.right", {"start": v(-112.48, -2.53) * mm, "end": v(-112.48, 2.53) * mm});
            skPoint(sketch, "E58.middle", {"position": v(-109.89, 0) * mm});
            skSolve(sketch);
        }
        {
            var Q0;
            Q0=qSketchRegion(id+"F30",true);
            extrude(context, id + "F31", {"entities" : qUnion([Q0]), "operationType" : NewBodyOperationType.ADD, "oppositeDirection" : true, "depth" : 10 * mm, "offsetDistance" : 25 * mm});
        }
        {
            var Q0;
            {var subQ0=sQuery(id+"F30.wireOp",EDGE,"E58.left");Q0=makeQuery(id+"F30.imprint","IMPRINT",FACE,{"disambiguationData":[TD([[makeQuery(id+"F30.imprint","IMPRINT",EDGE,{"derivedFrom":subQ0}),1.0]])]});}
            var sketch = newSketch(context, id + "F32", { "sketchPlane" : qUnion([Q0])});
            skCircle(sketch, "E59", {"center": v(-109.88, 0) * mm, "radius": 1.45 * mm});
            skSolve(sketch);
        }
        {
            var Q0;
            Q0=qSketchRegion(id+"F32",true);
            extrude(context, id + "F33", {"entities" : qUnion([Q0]), "operationType" : NewBodyOperationType.REMOVE, "oppositeDirection" : true, "depth" : 10 * mm, "offsetDistance" : 25 * mm});
        }
    });
